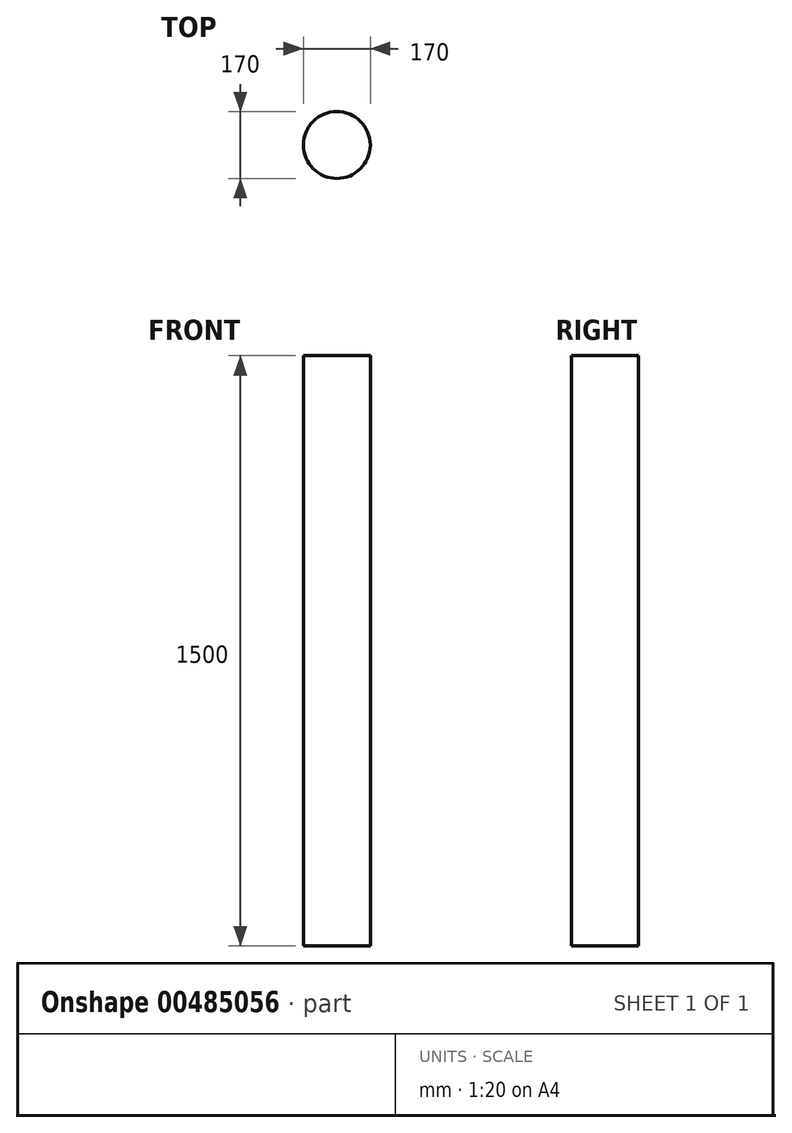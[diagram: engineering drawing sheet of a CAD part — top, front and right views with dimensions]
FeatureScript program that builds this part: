
annotation { "Feature Type Name" : "Feature", "Feature Type Description" : "" }
export const myFeature = defineFeature(function(context is Context, id is Id, definition is map)
    precondition{}
    {
        {
            var Q0;
            Q0=qCreatedBy(makeId("Top.planeOp"),FACE);
            var sketch = newSketch(context, id + "F0", { "sketchPlane" : qUnion([Q0])});
            skCircle(sketch, "E0", {"center": v(0, 0) * mm, "radius": 85 * mm});
            skSolve(sketch);
        }
        {
            var Q0;
            Q0 = qSketchRegion(id + "F0", true);
            extrude(context, id + "F1", {"entities" : qUnion([Q0]), "depth" : 1500 * mm});
        }
    });
